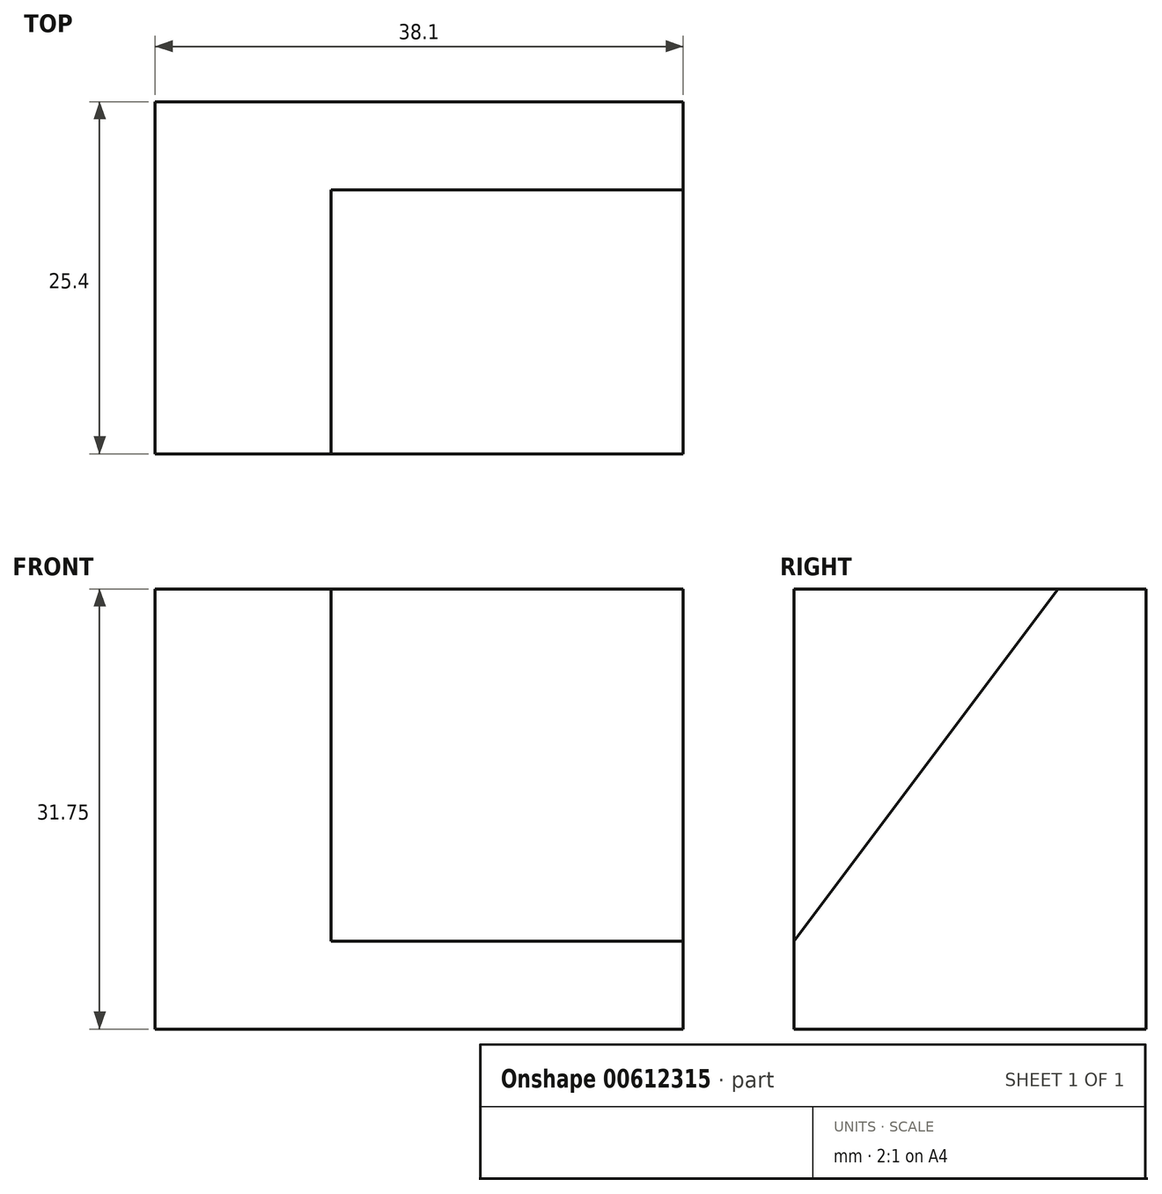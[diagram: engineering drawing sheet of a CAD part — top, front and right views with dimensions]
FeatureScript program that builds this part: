
annotation { "Feature Type Name" : "Feature", "Feature Type Description" : "" }
export const myFeature = defineFeature(function(context is Context, id is Id, definition is map)
    precondition{}
    {
        {
            var Q0;
            Q0=qCreatedBy(makeId("Front.planeOp"),FACE);
            var sketch = newSketch(context, id + "F0", { "sketchPlane" : qUnion([Q0])});
            skLineSegment(sketch, "E0", {"start": v(0, 0) * mm, "end": v(0, 31.75) * mm});
            skLineSegment(sketch, "E1", {"start": v(0, 31.75) * mm, "end": v(38.1, 31.75) * mm});
            skLineSegment(sketch, "E2", {"start": v(38.1, 31.75) * mm, "end": v(38.1, 0) * mm});
            skLineSegment(sketch, "E3", {"start": v(38.1, 0) * mm, "end": v(0, 0) * mm});
            skSolve(sketch);
        }
        {
            var Q0;
            Q0=makeQuery(id+"F0.imprint","IMPRINT",FACE,{"disambiguationData":[TD([[makeQuery(id+"F0.imprint","IMPRINT",EDGE,{"derivedFrom":sQuery(id+"F0.wireOp",EDGE,"E0")}),-1.0]])]});
            extrude(context, id + "F1", {"entities" : qUnion([Q0]), "depth" : 25.4 * mm});
        }
        {
            var Q0;
            Q0=makeQuery(id+"F1.opExtrude","SWEPT_FACE",FACE,{"disambiguationData":[OSD([sQuery(id+"F0.wireOp",EDGE,"E2")])]});
            var sketch = newSketch(context, id + "F2", { "sketchPlane" : qUnion([Q0])});
            skLineSegment(sketch, "E4", {"start": v(-6.35, 31.75) * mm, "end": v(-25.4, 6.35) * mm});
            skSolve(sketch);
        }
        {
            var Q0;
            Q0=qSketchRegion(id+"F2",true);
            var Q1;
            {var subQ0=sQuery(id+"F2.wireOp",EDGE,"E4");Q1=makeQuery(id+"F2.imprint","IMPRINT",FACE,{"disambiguationData":[TD([[makeQuery(id+"F2.imprint","IMPRINT",EDGE,{"derivedFrom":subQ0}),-1.0]])]});}
            extrude(context, id + "F3", {"entities" : qUnion([Q0, Q1]), "operationType" : NewBodyOperationType.REMOVE, "oppositeDirection" : true, "depth" : 25.4 * mm});
        }
    });
